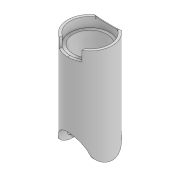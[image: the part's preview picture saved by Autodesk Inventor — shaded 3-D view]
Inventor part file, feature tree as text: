
AUTODESK INVENTOR PART (.ipt)
format: ipt  version: 2020 (Build 240168000, 168)  size: 285,696 bytes
history: native  units: mm
features: sketch x11, extrude x10, projected_geometry x3, revolve x2, plane x1
ambient origin geometry x8: Origin, YZ Plane, XZ Plane, XY Plane, X Axis, Y Axis, Z Axis, Center Point
bodies: Solid1 (feature_tree)
feature tree (27):
  revolve  "Revolution1"  [1 undecoded]
  extrude  "Extrusion1"  Depth=1.1184mm
  extrude  "Extrusion3"  Depth=12.5mm TaperAngle=0.0deg
  extrude  "Extrusion4"  Depth=1.93mm
  revolve  "Revolution2"  [1 undecoded]
  extrude  "Extrusion6"  Depth=24.534mm
  extrude  "Extrusion7"  Depth=4.6mm
  extrude  "Extrusion8"  Depth=4.6mm
  extrude  "Extrusion9"  Depth=0.62mm TaperAngle=0.0deg
  plane  "Work Plane2"
  extrude  "Extrusion11"  Depth=0.808mm
  extrude  "Extrusion12"  TaperAngle=90.0deg  [1 undecoded]
  extrude  "Extrusion14"  Depth=10.0mm
  sketch  "Sketch1"  dims[d0=10.33mm d10=2.3mm]
  sketch  "Sketch2"  dims[d11=1.2mm d12=1.1184mm]
  sketch  "Sketch4"  dims[d15=90.0deg d18=12.5mm d19=0.0mm]
  sketch  "Sketch5"  dims[d20=1.5mm d21=1.93mm]
  sketch  "Sketch7"  dims[d22=2.5mm d23=1.2mm]
  sketch  "Sketch8"  dims[d24=4.0mm d25=24.534mm]
  sketch  "Sketch9"  dims[d27=0.3547mm d28=4.6mm]
  sketch  "Sketch10"  dims[d29=3.99mm d32=4.6mm]
  sketch  "Sketch11"  dims[d33=0.62mm d34=12.5mm d35=0.0mm]
  projected_geometry  "Projected Loop2"
  sketch  "Sketch14"  dims[d36=0.01mm d37=0.0mm d43=0.808mm]
  projected_geometry  "Projected Loop3"
  sketch  "Sketch16"  dims[d44=1.4269mm d45=90.0deg d46=10.0mm d47=46.75mm d48=0.0mm d49=46.75mm d50=0.0mm d51=2.4mm d52=8.75mm d53=8.875mm d54=0.0mm d55=0.0mm d56=11.75mm d57=0.0mm d61=6.0mm d62=14.0mm d63=0.0mm d65=10.0mm d66=0.0mm d69=2.0mm d70=9.0mm d71=90.0deg d72=90.0deg d73=90.0deg d74=10.0mm d75=10.0mm d76=0.25mm d77=0.0mm]
  projected_geometry  "Projected Loop5"
note: 3 required parameter values undecoded (feature->parameter linkage not recoverable at this tier; creation-order binding heuristic only, values carry confidence <= 0.55)